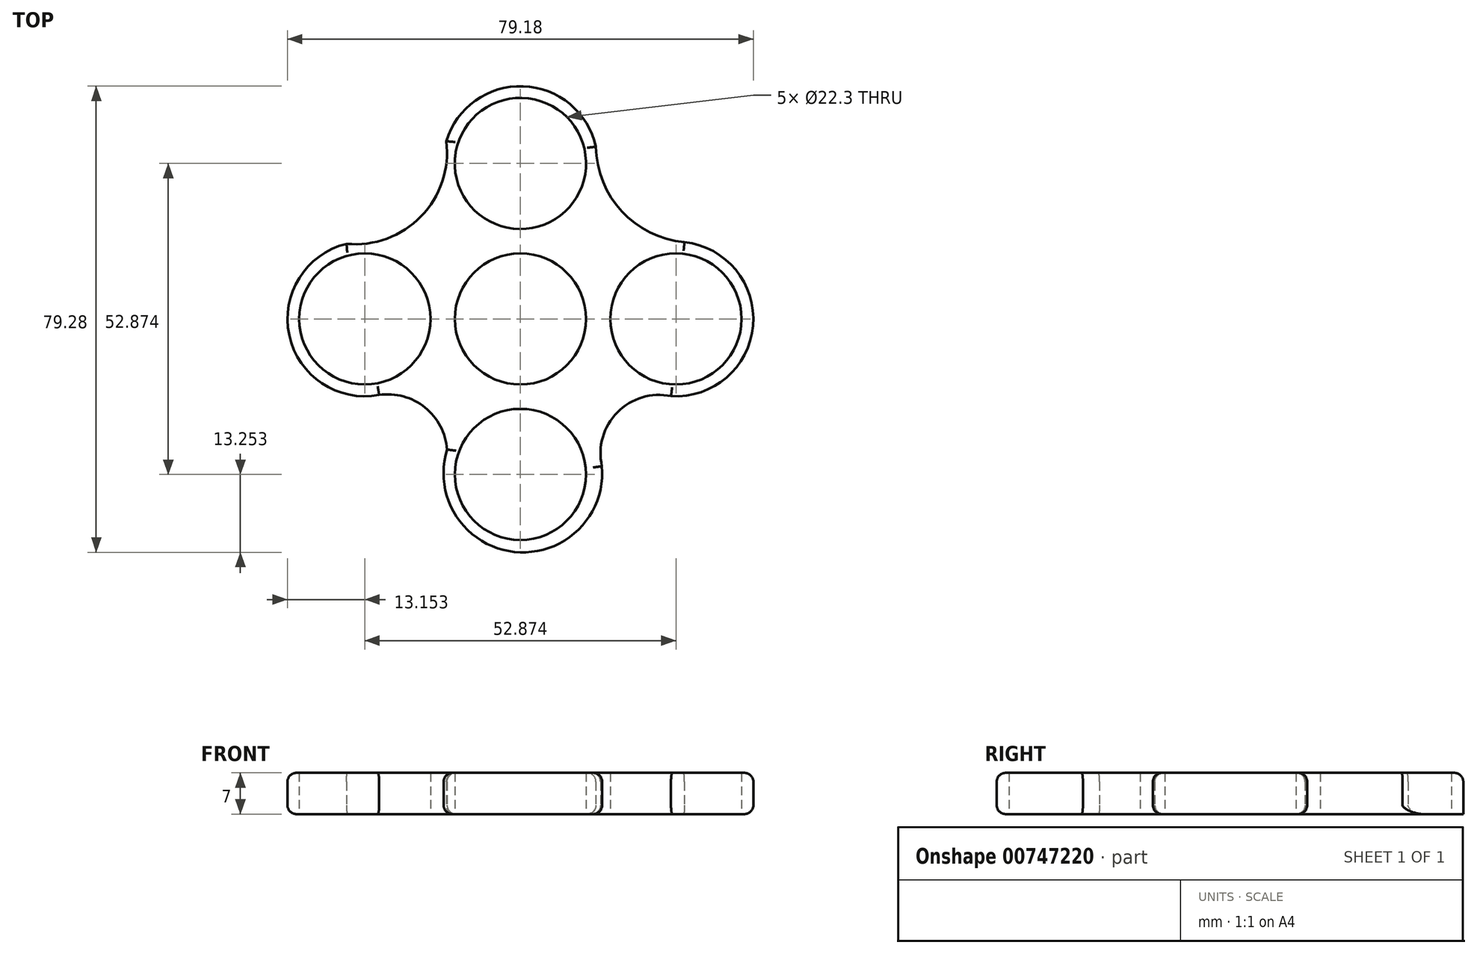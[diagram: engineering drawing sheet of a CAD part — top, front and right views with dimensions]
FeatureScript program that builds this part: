
annotation { "Feature Type Name" : "Feature", "Feature Type Description" : "" }
export const myFeature = defineFeature(function(context is Context, id is Id, definition is map)
    precondition{}
    {
        {
            var Q0;
            Q0=qCreatedBy(makeId("Top.planeOp"),FACE);
            var sketch = newSketch(context, id + "F0", { "sketchPlane" : qUnion([Q0])});
            skCircle(sketch, "E0", {"center": v(0, 0) * mm, "radius": 11.15 * mm});
            skCircle(sketch, "E1", {"center": v(0, 26.44) * mm, "radius": 11.15 * mm});
            skArc(sketch, "E2", {"start": v(13.15, 26.3) * mm, "mid": v(-0.98, 39.55) * mm, "end": v(-12.98, 24.35) * mm});
            skCircle(sketch, "E3.1.0", {"center": v(-26.44, 0) * mm, "radius": 11.15 * mm});
            skArc(sketch, "E3.1.1", {"start": v(-24.82, 13.05) * mm, "mid": v(-39.58, -0.41) * mm, "end": v(-24, -12.92) * mm});
            skCircle(sketch, "E3.2.0", {"center": v(0, -26.44) * mm, "radius": 11.15 * mm});
            skCircle(sketch, "E3.3.0", {"center": v(26.44, 0) * mm, "radius": 11.15 * mm});
            skArc(sketch, "E3.3.1", {"start": v(24, -12.92) * mm, "mid": v(39.46, -1.79) * mm, "end": v(27.56, 13.1) * mm});
            skArc(sketch, "E4", {"start": v(-29.55, 12.78) * mm, "mid": v(-16.89, 17.43) * mm, "end": v(-12.6, 30.22) * mm});
            skArc(sketch, "E5", {"start": v(12.84, 29.29) * mm, "mid": v(17.24, 18.29) * mm, "end": v(27.88, 13.07) * mm});
            skArc(sketch, "E6", {"start": v(25.6, -13.12) * mm, "mid": v(16.47, -15.88) * mm, "end": v(13.85, -25.04) * mm});
            skArc(sketch, "E7", {"start": v(-12.45, -22.22) * mm, "mid": v(-16.2, -15.05) * mm, "end": v(-24, -12.92) * mm});
            skArc(sketch, "E8", {"start": v(-12.45, -22.22) * mm, "mid": v(-1.02, -39.61) * mm, "end": v(13.85, -25.04) * mm});
            skSolve(sketch);
        }
        {
            var Q0;
            Q0=makeQuery(id+"F0.imprint","IMPRINT",FACE,{"disambiguationData":[TD([[makeQuery(id+"F0.imprint","IMPRINT",EDGE,{"derivedFrom":sQuery(id+"F0.wireOp",EDGE,"E0")}),-1.0]])]});
            extrude(context, id + "F1", {"entities" : qUnion([Q0]), "depth" : 7 * mm, "offsetDistance" : 25 * mm});
        }
        {
            var Q0;
            Q0=makeQuery(id+"F1.opExtrude","CAP_EDGE",EDGE,{"disambiguationData":[OSD([sQuery(id+"F0.wireOp",EDGE,"E7")])],"isStart":false});
            var Q1;
            Q1=makeQuery(id+"F1.opExtrude","CAP_EDGE",EDGE,{"disambiguationData":[OSD([sQuery(id+"F0.wireOp",EDGE,"E3.1.1")])],"isStart":false});
            var Q2;
            Q2=makeQuery(id+"F1.opExtrude","CAP_EDGE",EDGE,{"disambiguationData":[OSD([sQuery(id+"F0.wireOp",EDGE,"E4")])],"isStart":false});
            var Q3;
            Q3=makeQuery(id+"F1.opExtrude","CAP_EDGE",EDGE,{"disambiguationData":[OSD([sQuery(id+"F0.wireOp",EDGE,"E2")])],"isStart":false});
            var Q4;
            Q4=makeQuery(id+"F1.opExtrude","CAP_EDGE",EDGE,{"disambiguationData":[OSD([sQuery(id+"F0.wireOp",EDGE,"E5")])],"isStart":false});
            var Q5;
            Q5=makeQuery(id+"F1.opExtrude","CAP_EDGE",EDGE,{"disambiguationData":[OSD([sQuery(id+"F0.wireOp",EDGE,"E3.3.1")])],"isStart":false});
            var Q6;
            Q6=makeQuery(id+"F1.opExtrude","CAP_EDGE",EDGE,{"disambiguationData":[OSD([sQuery(id+"F0.wireOp",EDGE,"E6")])],"isStart":false});
            var Q7;
            Q7=makeQuery(id+"F1.opExtrude","CAP_EDGE",EDGE,{"disambiguationData":[OSD([sQuery(id+"F0.wireOp",EDGE,"E8")])],"isStart":false});
            var Q8;
            Q8=makeQuery(id+"F1.opExtrude","CAP_EDGE",EDGE,{"disambiguationData":[OSD([sQuery(id+"F0.wireOp",EDGE,"E4")])],"isStart":true});
            var Q9;
            Q9=makeQuery(id+"F1.opExtrude","CAP_EDGE",EDGE,{"disambiguationData":[OSD([sQuery(id+"F0.wireOp",EDGE,"E3.1.1")])],"isStart":true});
            var Q10;
            Q10=makeQuery(id+"F1.opExtrude","CAP_EDGE",EDGE,{"disambiguationData":[OSD([sQuery(id+"F0.wireOp",EDGE,"E7")])],"isStart":true});
            var Q11;
            Q11=makeQuery(id+"F1.opExtrude","CAP_EDGE",EDGE,{"disambiguationData":[OSD([sQuery(id+"F0.wireOp",EDGE,"E8")])],"isStart":true});
            var Q12;
            Q12=makeQuery(id+"F1.opExtrude","CAP_EDGE",EDGE,{"disambiguationData":[OSD([sQuery(id+"F0.wireOp",EDGE,"E6")])],"isStart":true});
            var Q13;
            Q13=makeQuery(id+"F1.opExtrude","CAP_EDGE",EDGE,{"disambiguationData":[OSD([sQuery(id+"F0.wireOp",EDGE,"E3.3.1")])],"isStart":true});
            var Q14;
            Q14=makeQuery(id+"F1.opExtrude","CAP_EDGE",EDGE,{"disambiguationData":[OSD([sQuery(id+"F0.wireOp",EDGE,"E5")])],"isStart":true});
            fillet(context, id + "F2", {"entities" : qUnion([Q0, Q1, Q2, Q3, Q4, Q5, Q6, Q7, Q8, Q9, Q10, Q11, Q12, Q13, Q14]), "radius" : 1.5 * mm, "tangentPropagation" : true, "allowEdgeOverflow" : false});
        }
    });
